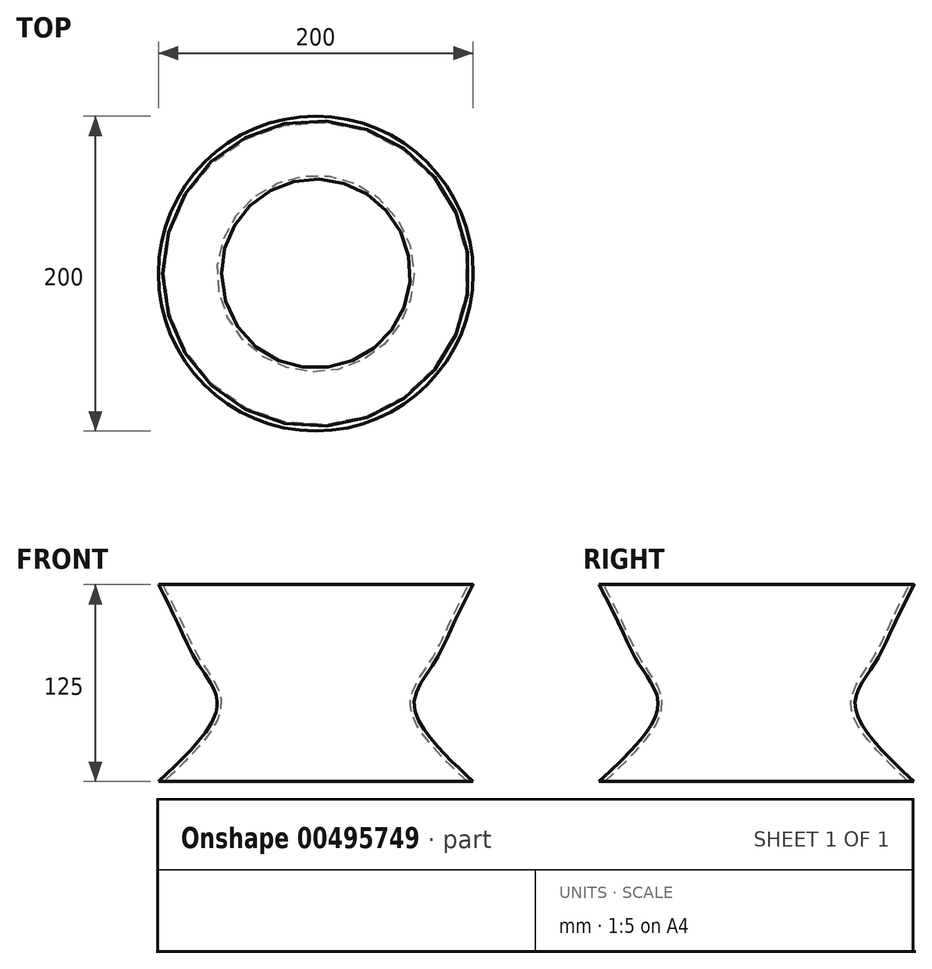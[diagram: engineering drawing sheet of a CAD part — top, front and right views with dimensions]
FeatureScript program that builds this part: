
annotation { "Feature Type Name" : "Feature", "Feature Type Description" : "" }
export const myFeature = defineFeature(function(context is Context, id is Id, definition is map)
    precondition{}
    {
        {
            var Q0;
            Q0=qCreatedBy(makeId("Top.planeOp"),FACE);
            cPlane(context, id + "F0", {"entities" : qUnion([Q0]), "cplaneType" : CPlaneType.OFFSET, "offset" : 25 * mm, "width" : 150 * mm, "height" : 150 * mm});
        }
        {
            var Q0;
            Q0=qCreatedBy(id+"F0.planeOp",FACE);
            cPlane(context, id + "F1", {"entities" : qUnion([Q0]), "cplaneType" : CPlaneType.OFFSET, "offset" : 25 * mm, "width" : 150 * mm, "height" : 150 * mm});
        }
        {
            var Q0;
            Q0=qCreatedBy(id+"F1.planeOp",FACE);
            cPlane(context, id + "F2", {"entities" : qUnion([Q0]), "cplaneType" : CPlaneType.OFFSET, "offset" : 25 * mm, "width" : 150 * mm, "height" : 150 * mm});
        }
        {
            var Q0;
            Q0=qCreatedBy(id+"F2.planeOp",FACE);
            cPlane(context, id + "F3", {"entities" : qUnion([Q0]), "cplaneType" : CPlaneType.OFFSET, "offset" : 25 * mm, "width" : 150 * mm, "height" : 150 * mm});
        }
        {
            var Q0;
            Q0=qCreatedBy(id+"F3.planeOp",FACE);
            cPlane(context, id + "F4", {"entities" : qUnion([Q0]), "cplaneType" : CPlaneType.OFFSET, "offset" : 25 * mm, "width" : 150 * mm, "height" : 150 * mm});
        }
        {
            var Q0;
            Q0=qCreatedBy(id+"F4.planeOp",FACE);
            var sketch = newSketch(context, id + "F5", { "sketchPlane" : qUnion([Q0])});
            skCircle(sketch, "E0", {"center": v(0, 0) * mm, "radius": 100 * mm});
            skSolve(sketch);
        }
        {
            var Q0;
            Q0=qCreatedBy(id+"F3.planeOp",FACE);
            var sketch = newSketch(context, id + "F6", { "sketchPlane" : qUnion([Q0])});
            skCircle(sketch, "E1", {"center": v(0, 0) * mm, "radius": 87.5 * mm});
            skSolve(sketch);
        }
        {
            var Q0;
            Q0=qCreatedBy(id+"F2.planeOp",FACE);
            var sketch = newSketch(context, id + "F7", { "sketchPlane" : qUnion([Q0])});
            skCircle(sketch, "E2", {"center": v(0, 0) * mm, "radius": 75 * mm});
            skSolve(sketch);
        }
        {
            var Q0;
            Q0=qCreatedBy(id+"F1.planeOp",FACE);
            var sketch = newSketch(context, id + "F8", { "sketchPlane" : qUnion([Q0])});
            skCircle(sketch, "E3", {"center": v(0, 0) * mm, "radius": 62.5 * mm});
            skSolve(sketch);
        }
        {
            var Q0;
            Q0=qCreatedBy(id+"F0.planeOp",FACE);
            var sketch = newSketch(context, id + "F9", { "sketchPlane" : qUnion([Q0])});
            skCircle(sketch, "E4", {"center": v(0, 0) * mm, "radius": 75 * mm});
            skSolve(sketch);
        }
        {
            var Q0;
            Q0=qCreatedBy(makeId("Top.planeOp"),FACE);
            var sketch = newSketch(context, id + "F10", { "sketchPlane" : qUnion([Q0])});
            skCircle(sketch, "E5", {"center": v(0, 0) * mm, "radius": 100 * mm});
            skSolve(sketch);
        }
        {
            var Q0;
            Q0=makeQuery(id+"F5.imprint","IMPRINT",FACE,{"disambiguationData":[TD([[makeQuery(id+"F5.imprint","IMPRINT",EDGE,{"derivedFrom":sQuery(id+"F5.wireOp",EDGE,"E0")}),1.0]])]});
            var Q1;
            Q1=makeQuery(id+"F6.imprint","IMPRINT",FACE,{"disambiguationData":[TD([[makeQuery(id+"F6.imprint","IMPRINT",EDGE,{"derivedFrom":sQuery(id+"F6.wireOp",EDGE,"E1")}),1.0]])]});
            var Q2;
            Q2=makeQuery(id+"F7.imprint","IMPRINT",FACE,{"disambiguationData":[TD([[makeQuery(id+"F7.imprint","IMPRINT",EDGE,{"derivedFrom":sQuery(id+"F7.wireOp",EDGE,"E2")}),1.0]])]});
            var Q3;
            Q3=makeQuery(id+"F8.imprint","IMPRINT",FACE,{"disambiguationData":[TD([[makeQuery(id+"F8.imprint","IMPRINT",EDGE,{"derivedFrom":sQuery(id+"F8.wireOp",EDGE,"E3")}),1.0]])]});
            var Q4;
            Q4=makeQuery(id+"F9.imprint","IMPRINT",FACE,{"disambiguationData":[TD([[makeQuery(id+"F9.imprint","IMPRINT",EDGE,{"derivedFrom":sQuery(id+"F9.wireOp",EDGE,"E4")}),1.0]])]});
            var Q5;
            Q5=makeQuery(id+"F10.imprint","IMPRINT",FACE,{"disambiguationData":[TD([[makeQuery(id+"F10.imprint","IMPRINT",EDGE,{"derivedFrom":sQuery(id+"F10.wireOp",EDGE,"E5")}),1.0]])]});
            loft(context, id + "F11", {"sheetProfilesArray" : [{ "sheetProfileEntities" : qUnion([Q0]) }, { "sheetProfileEntities" : qUnion([Q1]) }, { "sheetProfileEntities" : qUnion([Q2]) }, { "sheetProfileEntities" : qUnion([Q3]) }, { "sheetProfileEntities" : qUnion([Q4]) }, { "sheetProfileEntities" : qUnion([Q5]) }]});
        }
        {
            var Q0;
            Q0=makeQuery(id+"F11.opLoft","CAP_FACE",FACE,{"disambiguationData":[OSD([makeQuery(id+"F10.imprint","IMPRINT",FACE,{"disambiguationData":[TD([[makeQuery(id+"F10.imprint","IMPRINT",EDGE,{"derivedFrom":sQuery(id+"F10.wireOp",EDGE,"E5")}),1.0]])]})])],"isStart":true});
            var Q1;
            Q1=makeQuery(id+"F11.opLoft","CAP_FACE",FACE,{"disambiguationData":[OSD([makeQuery(id+"F5.imprint","IMPRINT",FACE,{"disambiguationData":[TD([[makeQuery(id+"F5.imprint","IMPRINT",EDGE,{"derivedFrom":sQuery(id+"F5.wireOp",EDGE,"E0")}),1.0]])]})])],"isStart":true});
            shell(context, id + "F12", {"entities" : qUnion([Q0, Q1]), "thickness" : 2.5 * mm});
        }
    });
